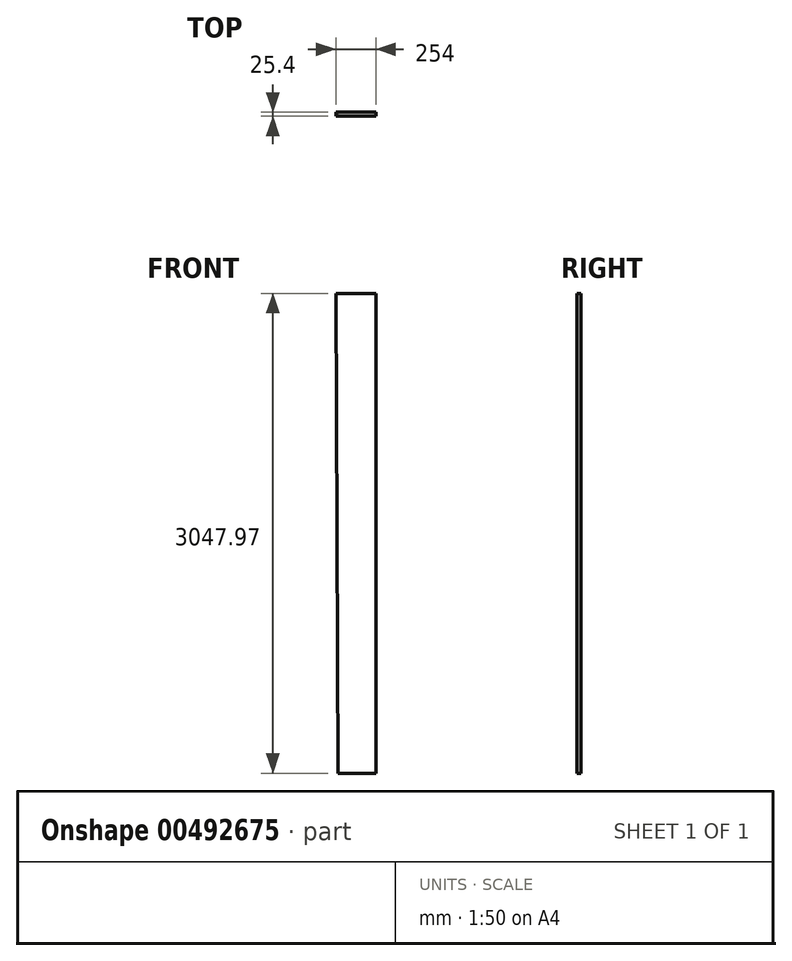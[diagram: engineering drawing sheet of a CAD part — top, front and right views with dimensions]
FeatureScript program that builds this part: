
annotation { "Feature Type Name" : "Feature", "Feature Type Description" : "" }
export const myFeature = defineFeature(function(context is Context, id is Id, definition is map)
    precondition{}
    {
        {
            var Q0;
            Q0=qCreatedBy(makeId("Front.planeOp"),FACE);
            var sketch = newSketch(context, id + "F0", { "sketchPlane" : qUnion([Q0])});
            skLineSegment(sketch, "E0", {"start": v(142.97, 1063.42) * mm, "end": v(142.97, -1984.55) * mm});
            skLineSegment(sketch, "E1", {"start": v(142.97, -1984.55) * mm, "end": v(-97.42, -1984.55) * mm});
            skLineSegment(sketch, "E2", {"start": v(142.97, 1063.42) * mm, "end": v(-111.03, 1063.42) * mm});
            skLineSegment(sketch, "E3", {"start": v(-111.03, 1063.42) * mm, "end": v(-97.42, -1984.55) * mm});
            skSolve(sketch);
        }
        {
            var Q0;
            Q0=makeQuery(id+"F0.imprint","IMPRINT",FACE,{"disambiguationData":[TD([[makeQuery(id+"F0.imprint","IMPRINT",EDGE,{"derivedFrom":sQuery(id+"F0.wireOp",EDGE,"E0")}),-1.0]])]});
            extrude(context, id + "F1", {"entities" : qUnion([Q0]), "depth" : 25.4 * mm});
        }
    });
